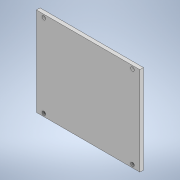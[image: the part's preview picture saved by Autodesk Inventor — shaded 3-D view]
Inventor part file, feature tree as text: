
AUTODESK INVENTOR PART (.ipt)
format: ipt  version: 2020.3 (Build 243373000, 373)  size: 111,616 bytes
history: native  units: mm
features: extrude x2, sketch x2
ambient origin geometry x8: Origin, YZ Plane, XZ Plane, XY Plane, X Axis, Y Axis, Z Axis, Center Point
bodies: Solid1 (feature_tree)
feature tree (4):
  extrude  "Extrusion1"  Depth=72.9mm
  extrude  "Extrusion2"  Depth=3.0mm
  sketch  "Sketch1"  dims[d0=85.0mm d1=72.9mm]
  sketch  "Sketch2"  dims[d2=3.0mm d3=0.0mm d4=3.0mm d5=3.0mm d6=3.0mm d7=6.072mm d8=2.5mm d9=2.5mm d10=6.072mm d11=2.5mm d12=6.072mm d13=6.072mm d14=2.5mm d15=10.0mm d16=0.0mm]
